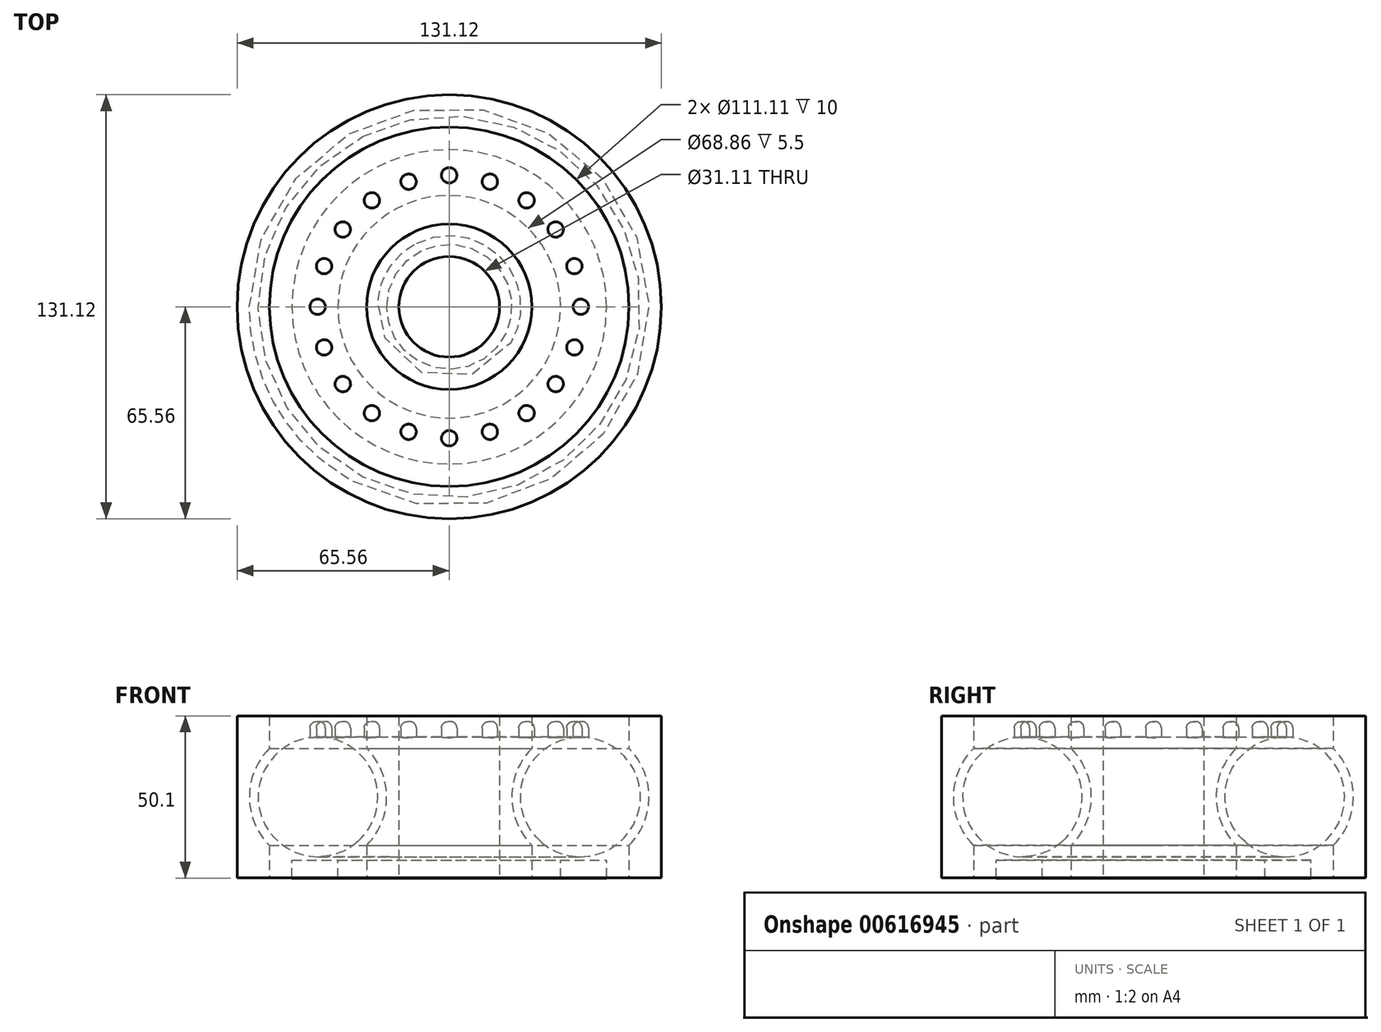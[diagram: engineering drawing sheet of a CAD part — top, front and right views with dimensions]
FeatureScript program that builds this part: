
annotation { "Feature Type Name" : "Feature", "Feature Type Description" : "" }
export const myFeature = defineFeature(function(context is Context, id is Id, definition is map)
    precondition{}
    {
        {
            var Q0;
            Q0=qCreatedBy(makeId("Front.planeOp"),FACE);
            var sketch = newSketch(context, id + "F0", { "sketchPlane" : qUnion([Q0])});
            skLineSegment(sketch, "E0", {"start": v(-65.56, 0) * mm, "end": v(-65.56, 50) * mm});
            skLineSegment(sketch, "E1", {"start": v(-15.56, 50) * mm, "end": v(-15.56, 0) * mm});
            skLineSegment(sketch, "E2", {"start": v(-65.56, 50) * mm, "end": v(-55.56, 50) * mm});
            skLineSegment(sketch, "E3", {"start": v(-65.56, 0) * mm, "end": v(-55.56, 0) * mm});
            skLineSegment(sketch, "E4", {"start": v(-15.56, 50) * mm, "end": v(-25.56, 50) * mm});
            skLineSegment(sketch, "E5", {"start": v(-15.56, 0) * mm, "end": v(-25.56, 0) * mm});
            skLineSegment(sketch, "E6", {"start": v(-55.56, 50) * mm, "end": v(-55.56, 40) * mm});
            skLineSegment(sketch, "E7", {"start": v(-55.56, 0) * mm, "end": v(-55.56, 10) * mm});
            skLineSegment(sketch, "E8", {"start": v(-25.56, 0) * mm, "end": v(-25.56, 10) * mm});
            skLineSegment(sketch, "E9", {"start": v(-25.56, 50) * mm, "end": v(-25.56, 40) * mm});
            skArc(sketch, "E10", {"start": v(-55.56, 40) * mm, "mid": v(-61.77, 25) * mm, "end": v(-55.56, 10) * mm});
            skArc(sketch, "E11", {"start": v(-25.56, 10) * mm, "mid": v(-19.34, 25) * mm, "end": v(-25.56, 40) * mm});
            skLineSegment(sketch, "E12", {"start": v(0, 0) * mm, "end": v(0, 21.39) * mm});
            skCircle(sketch, "E13", {"center": v(-40.56, 25) * mm, "radius": 18.5 * mm});
            skSolve(sketch);
        }
        {
            var Q0;
            Q0=makeQuery(id+"F0.imprint","IMPRINT",FACE,{"disambiguationData":[TD([[makeQuery(id+"F0.imprint","IMPRINT",EDGE,{"derivedFrom":sQuery(id+"F0.wireOp",EDGE,"E0")}),-1.0]])]});
            var Q1;
            Q1=makeQuery(id+"F0.imprint","IMPRINT",FACE,{"disambiguationData":[TD([[makeQuery(id+"F0.imprint","IMPRINT",EDGE,{"derivedFrom":sQuery(id+"F0.wireOp",EDGE,"E1")}),-1.0]])]});
            var Q2;
            Q2=sQuery(id+"F0.wireOp",EDGE,"E12");
            revolve(context, id + "F1", {"entities" : qUnion([Q0, Q1]), "axis" : qUnion([Q2]), "revolveType" : RevolveType.FULL});
        }
        {
            var Q0;
            Q0=makeQuery(id+"F0.imprint","IMPRINT",FACE,{"disambiguationData":[TD([[makeQuery(id+"F0.imprint","IMPRINT",EDGE,{"derivedFrom":sQuery(id+"F0.wireOp",EDGE,"E13")}),1.0]])]});
            var Q1;
            Q1=sQuery(id+"F0.wireOp",EDGE,"E12");
            revolve(context, id + "F2", {"entities" : qUnion([Q0]), "axis" : qUnion([Q1]), "revolveType" : RevolveType.FULL});
        }
        {
            var Q0;
            Q0=qCreatedBy(makeId("Top.planeOp"),FACE);
            cPlane(context, id + "F3", {"entities" : qUnion([Q0]), "cplaneType" : CPlaneType.OFFSET, "offset" : 43.3 * mm, "width" : 150 * mm, "height" : 150 * mm});
        }
        {
            var Q0;
            Q0=qCreatedBy(id+"F3.planeOp",FACE);
            var sketch = newSketch(context, id + "F4", { "sketchPlane" : qUnion([Q0])});
            skCircle(sketch, "E14", {"center": v(-40.66, 0) * mm, "radius": 2.38 * mm});
            skCircle(sketch, "E15.1.0", {"center": v(-38.67, -12.57) * mm, "radius": 2.38 * mm});
            skCircle(sketch, "E15.2.0", {"center": v(-32.9, -23.9) * mm, "radius": 2.38 * mm});
            skCircle(sketch, "E15.3.0", {"center": v(-23.9, -32.9) * mm, "radius": 2.38 * mm});
            skCircle(sketch, "E15.4.0", {"center": v(-12.57, -38.67) * mm, "radius": 2.38 * mm});
            skCircle(sketch, "E15.5.0", {"center": v(0, -40.66) * mm, "radius": 2.38 * mm});
            skCircle(sketch, "E15.6.0", {"center": v(12.57, -38.67) * mm, "radius": 2.38 * mm});
            skCircle(sketch, "E15.7.0", {"center": v(23.9, -32.9) * mm, "radius": 2.38 * mm});
            skCircle(sketch, "E15.8.0", {"center": v(32.9, -23.9) * mm, "radius": 2.38 * mm});
            skCircle(sketch, "E15.9.0", {"center": v(38.67, -12.57) * mm, "radius": 2.38 * mm});
            skCircle(sketch, "E15.10.0", {"center": v(40.66, 0) * mm, "radius": 2.38 * mm});
            skCircle(sketch, "E15.11.0", {"center": v(38.67, 12.57) * mm, "radius": 2.38 * mm});
            skCircle(sketch, "E15.12.0", {"center": v(32.9, 23.9) * mm, "radius": 2.38 * mm});
            skCircle(sketch, "E15.13.0", {"center": v(23.9, 32.9) * mm, "radius": 2.38 * mm});
            skCircle(sketch, "E15.14.0", {"center": v(12.57, 38.67) * mm, "radius": 2.38 * mm});
            skCircle(sketch, "E15.15.0", {"center": v(0, 40.66) * mm, "radius": 2.38 * mm});
            skCircle(sketch, "E15.16.0", {"center": v(-12.57, 38.67) * mm, "radius": 2.38 * mm});
            skCircle(sketch, "E15.17.0", {"center": v(-23.9, 32.9) * mm, "radius": 2.38 * mm});
            skCircle(sketch, "E15.18.0", {"center": v(-32.9, 23.9) * mm, "radius": 2.38 * mm});
            skCircle(sketch, "E15.19.0", {"center": v(-38.67, 12.57) * mm, "radius": 2.38 * mm});
            skPoint(sketch, "E15.center", {"position": v(0, 0) * mm});
            skSolve(sketch);
        }
        {
            var Q0;
            Q0 = qSketchRegion(id + "F4", true);
            extrude(context, id + "F5", {"entities" : qUnion([Q0]), "operationType" : NewBodyOperationType.ADD, "depth" : 5 * mm, "offsetDistance" : 25 * mm});
        }
        {
            var Q0;
            Q0=makeQuery(id+"F5.opExtrude","CAP_EDGE",EDGE,{"disambiguationData":[OSD([sQuery(id+"F4.wireOp",EDGE,"E15.9.0")])],"isStart":false});
            var Q1;
            Q1=makeQuery(id+"F5.opExtrude","CAP_EDGE",EDGE,{"disambiguationData":[OSD([sQuery(id+"F4.wireOp",EDGE,"E15.8.0")])],"isStart":false});
            var Q2;
            Q2=makeQuery(id+"F5.opExtrude","CAP_EDGE",EDGE,{"disambiguationData":[OSD([sQuery(id+"F4.wireOp",EDGE,"E15.7.0")])],"isStart":false});
            var Q3;
            Q3=makeQuery(id+"F5.opExtrude","CAP_EDGE",EDGE,{"disambiguationData":[OSD([sQuery(id+"F4.wireOp",EDGE,"E15.6.0")])],"isStart":false});
            var Q4;
            Q4=makeQuery(id+"F5.opExtrude","CAP_EDGE",EDGE,{"disambiguationData":[OSD([sQuery(id+"F4.wireOp",EDGE,"E15.5.0")])],"isStart":false});
            var Q5;
            Q5=makeQuery(id+"F5.opExtrude","CAP_FACE",FACE,{"disambiguationData":[OSD([sQuery(id+"F4.wireOp",EDGE,"E15.4.0")])],"isStart":false});
            var Q6;
            Q6=makeQuery(id+"F5.opExtrude","CAP_FACE",FACE,{"disambiguationData":[OSD([sQuery(id+"F4.wireOp",EDGE,"E15.3.0")])],"isStart":false});
            var Q7;
            Q7=makeQuery(id+"F5.opExtrude","CAP_FACE",FACE,{"disambiguationData":[OSD([sQuery(id+"F4.wireOp",EDGE,"E15.2.0")])],"isStart":false});
            var Q8;
            Q8=makeQuery(id+"F5.opExtrude","CAP_FACE",FACE,{"disambiguationData":[OSD([sQuery(id+"F4.wireOp",EDGE,"E15.1.0")])],"isStart":false});
            var Q9;
            Q9=makeQuery(id+"F5.opExtrude","CAP_FACE",FACE,{"disambiguationData":[OSD([sQuery(id+"F4.wireOp",EDGE,"E14")])],"isStart":false});
            var Q10;
            Q10=makeQuery(id+"F5.opExtrude","CAP_FACE",FACE,{"disambiguationData":[OSD([sQuery(id+"F4.wireOp",EDGE,"E15.19.0")])],"isStart":false});
            var Q11;
            Q11=makeQuery(id+"F5.opExtrude","CAP_FACE",FACE,{"disambiguationData":[OSD([sQuery(id+"F4.wireOp",EDGE,"E15.18.0")])],"isStart":false});
            var Q12;
            Q12=makeQuery(id+"F5.opExtrude","CAP_FACE",FACE,{"disambiguationData":[OSD([sQuery(id+"F4.wireOp",EDGE,"E15.17.0")])],"isStart":false});
            var Q13;
            Q13=makeQuery(id+"F5.opExtrude","CAP_EDGE",EDGE,{"disambiguationData":[OSD([sQuery(id+"F4.wireOp",EDGE,"E15.16.0")])],"isStart":false});
            var Q14;
            Q14=makeQuery(id+"F5.opExtrude","CAP_EDGE",EDGE,{"disambiguationData":[OSD([sQuery(id+"F4.wireOp",EDGE,"E15.15.0")])],"isStart":false});
            var Q15;
            Q15=makeQuery(id+"F5.opExtrude","CAP_FACE",FACE,{"disambiguationData":[OSD([sQuery(id+"F4.wireOp",EDGE,"E15.14.0")])],"isStart":false});
            var Q16;
            Q16=makeQuery(id+"F5.opExtrude","CAP_FACE",FACE,{"disambiguationData":[OSD([sQuery(id+"F4.wireOp",EDGE,"E15.13.0")])],"isStart":false});
            var Q17;
            Q17=makeQuery(id+"F5.opExtrude","CAP_FACE",FACE,{"disambiguationData":[OSD([sQuery(id+"F4.wireOp",EDGE,"E15.12.0")])],"isStart":false});
            var Q18;
            Q18=makeQuery(id+"F5.opExtrude","CAP_FACE",FACE,{"disambiguationData":[OSD([sQuery(id+"F4.wireOp",EDGE,"E15.11.0")])],"isStart":false});
            var Q19;
            Q19=makeQuery(id+"F5.opExtrude","CAP_FACE",FACE,{"disambiguationData":[OSD([sQuery(id+"F4.wireOp",EDGE,"E15.10.0")])],"isStart":false});
            fillet(context, id + "F6", {"entities" : qUnion([Q0, Q1, Q2, Q3, Q4, Q5, Q6, Q7, Q8, Q9, Q10, Q11, Q12, Q13, Q14, Q15, Q16, Q17, Q18, Q19]), "radius" : 2 * mm, "tangentPropagation" : true, "allowEdgeOverflow" : false});
        }
        {
            var Q0;
            Q0=makeQuery(id+"F1.opRevolve","SWEPT_FACE",FACE,{"disambiguationData":[OSD([sQuery(id+"F0.wireOp",EDGE,"E3")])]});
            cPlane(context, id + "F7", {"entities" : qUnion([Q0]), "cplaneType" : CPlaneType.OFFSET, "offset" : 5.4 * mm, "oppositeDirection" : true, "width" : 150 * mm, "height" : 150 * mm});
        }
        {
            var Q0;
            Q0=qCreatedBy(id+"F7.planeOp",FACE);
            var sketch = newSketch(context, id + "F8", { "sketchPlane" : qUnion([Q0])});
            skCircle(sketch, "E16", {"center": v(0, 0) * mm, "radius": 34.43 * mm});
            skCircle(sketch, "E17", {"center": v(0, 0) * mm, "radius": 48.61 * mm});
            skSolve(sketch);
        }
        {
            var Q0;
            Q0=makeQuery(id+"F8.imprint","IMPRINT",FACE,{"disambiguationData":[TD([[makeQuery(id+"F8.imprint","IMPRINT",EDGE,{"derivedFrom":sQuery(id+"F8.wireOp",EDGE,"E16")}),-1.0]])]});
            extrude(context, id + "F9", {"entities" : qUnion([Q0]), "depth" : 5.5 * mm, "offsetDistance" : 25 * mm});
        }
    });
